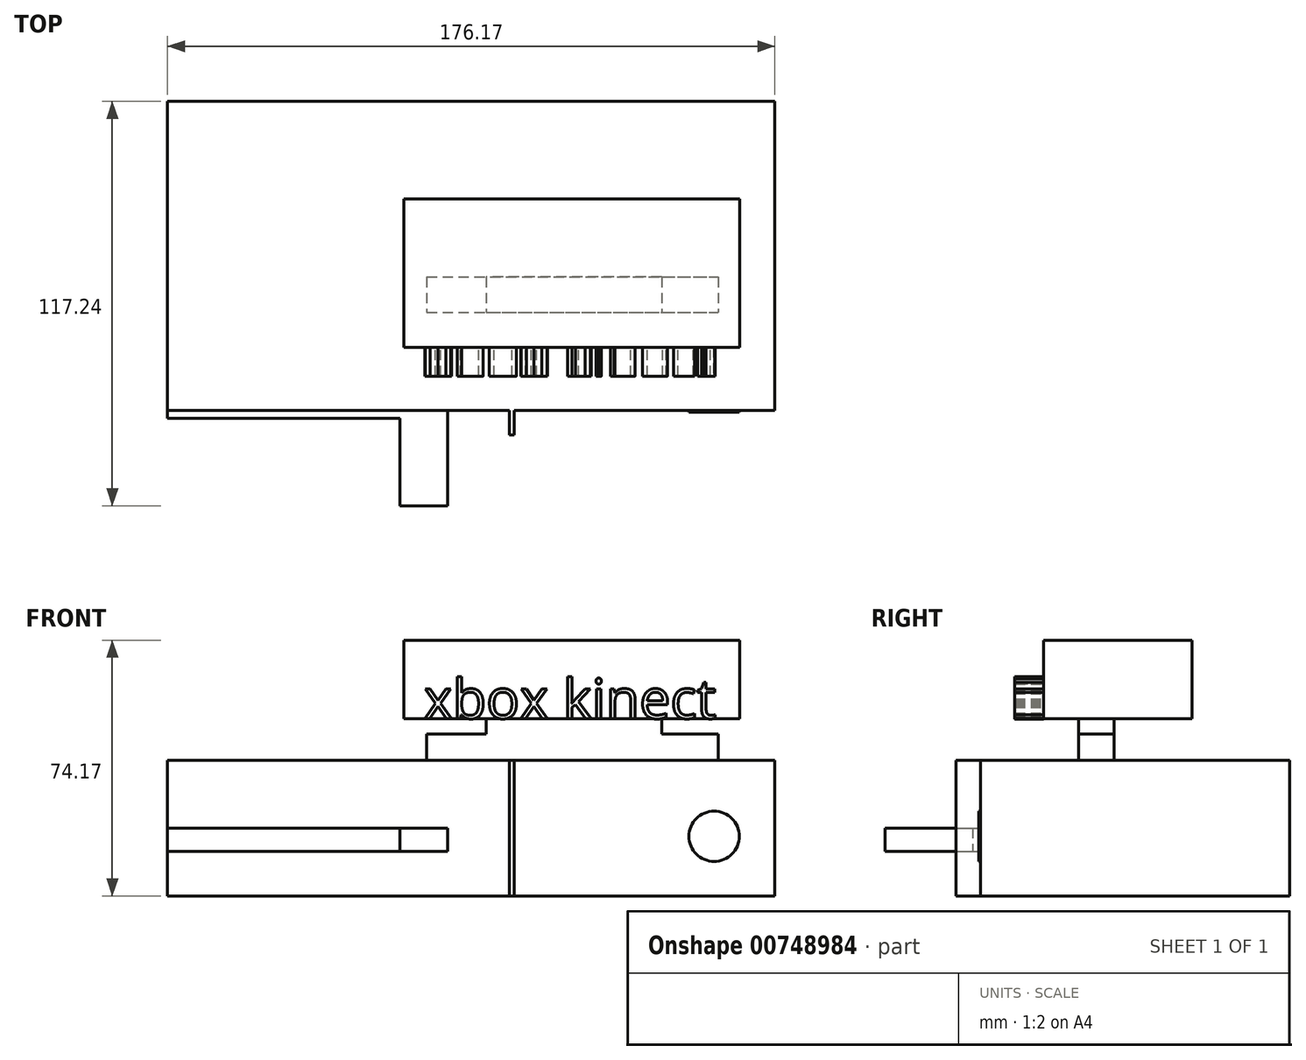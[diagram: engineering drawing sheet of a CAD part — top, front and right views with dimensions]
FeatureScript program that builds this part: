
annotation { "Feature Type Name" : "Feature", "Feature Type Description" : "" }
export const myFeature = defineFeature(function(context is Context, id is Id, definition is map)
    precondition{}
    {
        {
            var Q0;
            Q0=qCreatedBy(makeId("Top.planeOp"),FACE);
            var sketch = newSketch(context, id + "F0", { "sketchPlane" : qUnion([Q0])});
            skLineSegment(sketch, "E0.bottom", {"start": v(-150.59, 27.34) * mm, "end": v(25.58, 27.34) * mm});
            skLineSegment(sketch, "E0.top", {"start": v(-150.59, -62.22) * mm, "end": v(25.58, -62.22) * mm});
            skLineSegment(sketch, "E0.left", {"start": v(-150.59, 27.34) * mm, "end": v(-150.59, -62.22) * mm});
            skLineSegment(sketch, "E0.right", {"start": v(25.58, 27.34) * mm, "end": v(25.58, -62.22) * mm});
            skSolve(sketch);
        }
        {
            var Q0;
            Q0 = qSketchRegion(id + "F0", true);
            extrude(context, id + "F1", {"entities" : qUnion([Q0]), "depth" : 39.37 * mm, "offsetDistance" : 25.4 * mm});
        }
        {
            var Q0;
            Q0=makeQuery(id+"F1.opExtrude","SWEPT_FACE",FACE,{"disambiguationData":[OSD([sQuery(id+"F0.wireOp",EDGE,"E0.top")])]});
            var sketch = newSketch(context, id + "F2", { "sketchPlane" : qUnion([Q0])});
            skLineSegment(sketch, "E1.bottom", {"start": v(-150.59, 19.69) * mm, "end": v(-69.38, 19.69) * mm});
            skLineSegment(sketch, "E1.top", {"start": v(-150.59, 12.94) * mm, "end": v(-69.38, 12.94) * mm});
            skLineSegment(sketch, "E1.left", {"start": v(-150.59, 19.69) * mm, "end": v(-150.59, 12.94) * mm});
            skLineSegment(sketch, "E1.right", {"start": v(-69.38, 19.69) * mm, "end": v(-69.38, 12.94) * mm});
            skSolve(sketch);
        }
        {
            var Q0;
            Q0 = qSketchRegion(id + "F2", true);
            extrude(context, id + "F3", {"entities" : qUnion([Q0]), "operationType" : NewBodyOperationType.ADD, "depth" : 2.3 * mm, "offsetDistance" : 25.4 * mm});
        }
        {
            var Q0;
            Q0=makeQuery(id+"F1.opExtrude","SWEPT_FACE",FACE,{"disambiguationData":[OSD([sQuery(id+"F0.wireOp",EDGE,"E0.top")])]});
            var sketch = newSketch(context, id + "F4", { "sketchPlane" : qUnion([Q0])});
            skCircle(sketch, "E2", {"center": v(7.94, 17.3) * mm, "radius": 7.3 * mm});
            skSolve(sketch);
        }
        {
            var Q0;
            Q0 = qSketchRegion(id + "F4", true);
            extrude(context, id + "F5", {"entities" : qUnion([Q0]), "operationType" : NewBodyOperationType.ADD, "depth" : 0.5 * mm, "offsetDistance" : 25.4 * mm});
        }
        {
            var Q0;
            Q0=makeQuery(id+"F1.opExtrude","CAP_FACE",FACE,{"disambiguationData":[OSD([sQuery(id+"F0.wireOp",EDGE,"E0.bottom"),sQuery(id+"F0.wireOp",EDGE,"E0.top"),sQuery(id+"F0.wireOp",EDGE,"E0.left"),sQuery(id+"F0.wireOp",EDGE,"E0.right")])],"isStart":false});
            var sketch = newSketch(context, id + "F6", { "sketchPlane" : qUnion([Q0])});
            skText(sketch, "E3", { "text": "xbox one", "fontName": "OpenSans-Regular.ttf"});
            const initialGuessF6  = {"E3": [-0.14363, -0.05804, 1, 0, 0.0093]};
            skSetInitialGuess(sketch, initialGuessF6);
            skSolve(sketch);
        }
        {
            var Q0;
            Q0=makeQuery(id+"F6.imprint","IMPRINT",FACE,{"disambiguationData":[TD([[makeQuery(id+"F6.imprint","IMPRINT",EDGE,{"derivedFrom":sQuery(id+"F6.wireOp",EDGE,"E3.sketch_text.stroke-0")}),1.0]])]});
            var sketch = newSketch(context, id + "F7", { "sketchPlane" : qUnion([Q0])});
            skLineSegment(sketch, "E4.bottom", {"start": v(-75.4, -23.59) * mm, "end": v(9.16, -23.59) * mm});
            skLineSegment(sketch, "E4.top", {"start": v(-75.4, -33.78) * mm, "end": v(9.16, -33.78) * mm});
            skLineSegment(sketch, "E4.left", {"start": v(-75.4, -23.59) * mm, "end": v(-75.4, -33.78) * mm});
            skLineSegment(sketch, "E4.right", {"start": v(9.16, -23.59) * mm, "end": v(9.16, -33.78) * mm});
            skSolve(sketch);
        }
        {
            var Q0;
            Q0 = qSketchRegion(id + "F7", true);
            extrude(context, id + "F8", {"entities" : qUnion([Q0]), "operationType" : NewBodyOperationType.ADD, "depth" : 7.62 * mm, "offsetDistance" : 25.4 * mm});
        }
        {
            var Q0;
            Q0=makeQuery(id+"F8.opExtrude","CAP_FACE",FACE,{"disambiguationData":[OSD([sQuery(id+"F7.wireOp",EDGE,"E4.bottom"),sQuery(id+"F7.wireOp",EDGE,"E4.top"),sQuery(id+"F7.wireOp",EDGE,"E4.left"),sQuery(id+"F7.wireOp",EDGE,"E4.right")])],"isStart":false});
            var sketch = newSketch(context, id + "F9", { "sketchPlane" : qUnion([Q0])});
            skLineSegment(sketch, "E5.bottom", {"start": v(-58.14, -23.59) * mm, "end": v(-7.28, -23.59) * mm});
            skLineSegment(sketch, "E5.top", {"start": v(-58.14, -33.78) * mm, "end": v(-7.28, -33.78) * mm});
            skLineSegment(sketch, "E5.left", {"start": v(-58.14, -23.59) * mm, "end": v(-58.14, -33.78) * mm});
            skLineSegment(sketch, "E5.right", {"start": v(-7.28, -23.59) * mm, "end": v(-7.28, -33.78) * mm});
            skSolve(sketch);
        }
        {
            var Q0;
            Q0 = qSketchRegion(id + "F9", true);
            extrude(context, id + "F10", {"entities" : qUnion([Q0]), "operationType" : NewBodyOperationType.ADD, "depth" : 8.9 * mm, "offsetDistance" : 25.4 * mm});
        }
        {
            var Q0;
            Q0=makeQuery(id+"F10.boolean.opBoolean","MERGE",FACE,{"derivedFrom":[makeQuery(id+"F8.opExtrude","SWEPT_FACE",FACE,{"disambiguationData":[OSD([sQuery(id+"F7.wireOp",EDGE,"E4.top")])]}),makeQuery(id+"F10.opExtrude","SWEPT_FACE",FACE,{"disambiguationData":[OSD([sQuery(id+"F9.wireOp",EDGE,"E5.top")])]})]});
            var sketch = newSketch(context, id + "F11", { "sketchPlane" : qUnion([Q0])});
            skLineSegment(sketch, "E6.bottom", {"start": v(-58.14, 51.44) * mm, "end": v(-7.28, 51.44) * mm});
            skLineSegment(sketch, "E6.top", {"start": v(-58.14, 55.88) * mm, "end": v(-7.28, 55.88) * mm});
            skLineSegment(sketch, "E6.left", {"start": v(-58.14, 51.44) * mm, "end": v(-58.14, 55.88) * mm});
            skLineSegment(sketch, "E6.right", {"start": v(-7.28, 51.44) * mm, "end": v(-7.28, 55.88) * mm});
            skSolve(sketch);
        }
        {
            var Q0;
            Q0 = qSketchRegion(id + "F11", true);
            extrude(context, id + "F12", {"entities" : qUnion([Q0]), "operationType" : NewBodyOperationType.ADD, "depth" : 10.16 * mm, "offsetDistance" : 25.4 * mm});
        }
        {
            var Q0;
            Q0=makeQuery(id+"F10.boolean.opBoolean","MERGE",FACE,{"derivedFrom":[makeQuery(id+"F8.opExtrude","SWEPT_FACE",FACE,{"disambiguationData":[OSD([sQuery(id+"F7.wireOp",EDGE,"E4.bottom")])]}),makeQuery(id+"F10.opExtrude","SWEPT_FACE",FACE,{"disambiguationData":[OSD([sQuery(id+"F9.wireOp",EDGE,"E5.bottom")])]})]});
            var sketch = newSketch(context, id + "F13", { "sketchPlane" : qUnion([Q0])});
            skLineSegment(sketch, "E7.bottom", {"start": v(7.28, 51.44) * mm, "end": v(58.14, 51.44) * mm});
            skLineSegment(sketch, "E7.top", {"start": v(7.28, 55.88) * mm, "end": v(58.14, 55.88) * mm});
            skLineSegment(sketch, "E7.left", {"start": v(7.28, 51.44) * mm, "end": v(7.28, 55.88) * mm});
            skLineSegment(sketch, "E7.right", {"start": v(58.14, 51.44) * mm, "end": v(58.14, 55.88) * mm});
            skSolve(sketch);
        }
        {
            var Q0;
            Q0 = qSketchRegion(id + "F13", true);
            extrude(context, id + "F14", {"entities" : qUnion([Q0]), "operationType" : NewBodyOperationType.ADD, "depth" : 22.6 * mm, "offsetDistance" : 25.4 * mm});
        }
        {
            var Q0;
            Q0=makeQuery(id+"F14.boolean.opBoolean","MERGE",FACE,{"derivedFrom":[makeQuery(id+"F12.boolean.opBoolean","MERGE",FACE,{"derivedFrom":[makeQuery(id+"F10.opExtrude","CAP_FACE",FACE,{"disambiguationData":[OSD([sQuery(id+"F9.wireOp",EDGE,"E5.bottom"),sQuery(id+"F9.wireOp",EDGE,"E5.top"),sQuery(id+"F9.wireOp",EDGE,"E5.left"),sQuery(id+"F9.wireOp",EDGE,"E5.right")])],"isStart":false}),makeQuery(id+"F12.opExtrude","SWEPT_FACE",FACE,{"disambiguationData":[OSD([sQuery(id+"F11.wireOp",EDGE,"E6.top")])]})]}),makeQuery(id+"F14.opExtrude","SWEPT_FACE",FACE,{"disambiguationData":[OSD([sQuery(id+"F13.wireOp",EDGE,"E7.top")])]})]});
            extrude(context, id + "F15", {"entities" : qUnion([Q0]), "operationType" : NewBodyOperationType.ADD, "depth" : 18.29 * mm, "offsetDistance" : 25.4 * mm});
        }
        {
            var Q0;
            {var subQ0=sQuery(id+"F13.wireOp",EDGE,"E7.left");var subQ1=sQuery(id+"F11.wireOp",EDGE,"E6.right");var subQ2=sQuery(id+"F9.wireOp",EDGE,"E5.right");Q0=makeQuery(id+"F15.boolean.opBoolean","MERGE",FACE,{"derivedFrom":[makeQuery(id+"F14.boolean.opBoolean","MERGE",FACE,{"derivedFrom":[makeQuery(id+"F12.boolean.opBoolean","MERGE",FACE,{"derivedFrom":[makeQuery(id+"F10.opExtrude","SWEPT_FACE",FACE,{"disambiguationData":[OSD([subQ2])]}),makeQuery(id+"F12.opExtrude","SWEPT_FACE",FACE,{"disambiguationData":[OSD([subQ1])]})]}),makeQuery(id+"F14.opExtrude","SWEPT_FACE",FACE,{"disambiguationData":[OSD([subQ0])]})]}),makeQuery(id+"F15.opExtrude","SWEPT_FACE",FACE,{"disambiguationData":[OSD([subQ2,sQuery(id+"F11.wireOp",EDGE,"E6.top"),subQ1,sQuery(id+"F13.wireOp",EDGE,"E7.top"),subQ0])]})]});}
            var sketch = newSketch(context, id + "F16", { "sketchPlane" : qUnion([Q0])});
            skLineSegment(sketch, "E8.bottom", {"start": v(-43.94, 74.17) * mm, "end": v(-0.98, 74.17) * mm});
            skLineSegment(sketch, "E8.top", {"start": v(-43.94, 51.44) * mm, "end": v(-0.98, 51.44) * mm});
            skLineSegment(sketch, "E8.left", {"start": v(-43.94, 74.17) * mm, "end": v(-43.94, 51.44) * mm});
            skLineSegment(sketch, "E8.right", {"start": v(-0.98, 74.17) * mm, "end": v(-0.98, 51.44) * mm});
            skSolve(sketch);
        }
        {
            var Q0;
            Q0 = qSketchRegion(id + "F16", true);
            extrude(context, id + "F17", {"entities" : qUnion([Q0]), "operationType" : NewBodyOperationType.ADD, "depth" : 22.6 * mm, "offsetDistance" : 25.4 * mm});
        }
        {
            var Q0;
            {var subQ0=sQuery(id+"F13.wireOp",EDGE,"E7.right");var subQ1=sQuery(id+"F11.wireOp",EDGE,"E6.left");var subQ2=sQuery(id+"F9.wireOp",EDGE,"E5.left");Q0=makeQuery(id+"F15.boolean.opBoolean","MERGE",FACE,{"derivedFrom":[makeQuery(id+"F14.boolean.opBoolean","MERGE",FACE,{"derivedFrom":[makeQuery(id+"F12.boolean.opBoolean","MERGE",FACE,{"derivedFrom":[makeQuery(id+"F10.opExtrude","SWEPT_FACE",FACE,{"disambiguationData":[OSD([subQ2])]}),makeQuery(id+"F12.opExtrude","SWEPT_FACE",FACE,{"disambiguationData":[OSD([subQ1])]})]}),makeQuery(id+"F14.opExtrude","SWEPT_FACE",FACE,{"disambiguationData":[OSD([subQ0])]})]}),makeQuery(id+"F15.opExtrude","SWEPT_FACE",FACE,{"disambiguationData":[OSD([subQ2,sQuery(id+"F11.wireOp",EDGE,"E6.top"),subQ1,sQuery(id+"F13.wireOp",EDGE,"E7.top"),subQ0])]})]});}
            var sketch = newSketch(context, id + "F18", { "sketchPlane" : qUnion([Q0])});
            skLineSegment(sketch, "E9.bottom", {"start": v(0.98, 74.17) * mm, "end": v(43.94, 74.17) * mm});
            skLineSegment(sketch, "E9.top", {"start": v(0.98, 51.44) * mm, "end": v(43.94, 51.44) * mm});
            skLineSegment(sketch, "E9.left", {"start": v(0.98, 74.17) * mm, "end": v(0.98, 51.44) * mm});
            skLineSegment(sketch, "E9.right", {"start": v(43.94, 74.17) * mm, "end": v(43.94, 51.44) * mm});
            skSolve(sketch);
        }
        {
            var Q0;
            Q0 = qSketchRegion(id + "F18", true);
            extrude(context, id + "F19", {"entities" : qUnion([Q0]), "operationType" : NewBodyOperationType.ADD, "depth" : 23.88 * mm, "offsetDistance" : 25.4 * mm});
        }
        {
            var Q0;
            {var subQ0=sQuery(id+"F11.wireOp",EDGE,"E6.top");Q0=makeQuery(id+"F19.boolean.opBoolean","MERGE",FACE,{"derivedFrom":[makeQuery(id+"F17.boolean.opBoolean","MERGE",FACE,{"derivedFrom":[makeQuery(id+"F15.boolean.opBoolean","MERGE",FACE,{"derivedFrom":[makeQuery(id+"F12.opExtrude","CAP_FACE",FACE,{"disambiguationData":[OSD([sQuery(id+"F11.wireOp",EDGE,"E6.bottom"),subQ0,sQuery(id+"F11.wireOp",EDGE,"E6.left"),sQuery(id+"F11.wireOp",EDGE,"E6.right")])],"isStart":false}),makeQuery(id+"F15.opExtrude","SWEPT_FACE",FACE,{"disambiguationData":[OSD([subQ0])]})]}),makeQuery(id+"F17.opExtrude","SWEPT_FACE",FACE,{"disambiguationData":[OSD([sQuery(id+"F16.wireOp",EDGE,"E8.left")])]})]}),makeQuery(id+"F19.opExtrude","SWEPT_FACE",FACE,{"disambiguationData":[OSD([sQuery(id+"F18.wireOp",EDGE,"E9.right")])]})]});}
            var sketch = newSketch(context, id + "F20", { "sketchPlane" : qUnion([Q0])});
            skText(sketch, "E10", { "text": "xbox kinect", "fontName": "OpenSans-Regular.ttf"});
            const initialGuessF20  = {"E10": [-0.07631, 0.05144, 1, 0, 0.01151]};
            skSetInitialGuess(sketch, initialGuessF20);
            skSolve(sketch);
        }
        {
            var Q0;
            Q0 = qSketchRegion(id + "F20", true);
            extrude(context, id + "F21", {"entities" : qUnion([Q0]), "operationType" : NewBodyOperationType.ADD, "depth" : 8.38 * mm, "offsetDistance" : 25.4 * mm});
        }
        {
            var Q0;
            Q0=makeQuery(id+"F1.opExtrude","SWEPT_FACE",FACE,{"disambiguationData":[OSD([sQuery(id+"F0.wireOp",EDGE,"E0.top")])]});
            var sketch = newSketch(context, id + "F22", { "sketchPlane" : qUnion([Q0])});
            skText(sketch, "E11", { "text": "xbox one", "fontName": "OpenSans-Regular.ttf"});
            const initialGuessF22  = {"E11": [-0.1451, 0.02439, 1, 0, 0.00878]};
            skSetInitialGuess(sketch, initialGuessF22);
            skSolve(sketch);
        }
        {
            var Q0;
            {var subQ0=sQuery(id+"F0.wireOp",EDGE,"E0.left");var subQ2=sQuery(id+"F0.wireOp",EDGE,"E0.top");Q0=makeQuery(id+"FrHqVm97nXn3FNT_1.boolean.opBoolean","SPLIT",FACE,{"disambiguationData":[TD([makeQuery(id+"F1.opExtrude","SWEPT_FACE",FACE,{"disambiguationData":[OSD([subQ0])]})])],"derivedFrom":makeQuery(id+"F1.opExtrude","SWEPT_FACE",FACE,{"disambiguationData":[OSD([subQ2])]})});}
            var sketch = newSketch(context, id + "F23", { "sketchPlane" : qUnion([Q0])});
            skLineSegment(sketch, "E12.bottom", {"start": v(-50.11, 39.37) * mm, "end": v(-51.4, 39.37) * mm});
            skLineSegment(sketch, "E12.top", {"start": v(-50.11, 0) * mm, "end": v(-51.4, 0) * mm});
            skLineSegment(sketch, "E12.left", {"start": v(-50.11, 39.37) * mm, "end": v(-50.11, 0) * mm});
            skLineSegment(sketch, "E12.right", {"start": v(-51.4, 39.37) * mm, "end": v(-51.4, 0) * mm});
            skSolve(sketch);
        }
        {
            var Q0;
            Q0 = qSketchRegion(id + "F23", true);
            extrude(context, id + "F24", {"entities" : qUnion([Q0]), "operationType" : NewBodyOperationType.ADD, "depth" : 7.11 * mm, "offsetDistance" : 25.4 * mm});
        }
        {
            var Q0;
            Q0 = qSketchRegion(id + "F22", true);
            extrude(context, id + "F25", {"entities" : qUnion([Q0]), "operationType" : NewBodyOperationType.ADD, "oppositeDirection" : true, "depth" : 2.3 * mm, "offsetDistance" : 25.4 * mm});
        }
        {
            var Q0;
            {var subQ1=sQuery(id+"F0.wireOp",EDGE,"E0.left");var subQ2=sQuery(id+"F0.wireOp",EDGE,"E0.top");Q0=makeQuery(id+"F24.boolean.opBoolean","SPLIT",FACE,{"disambiguationData":[TD([makeQuery(id+"F1.opExtrude","SWEPT_FACE",FACE,{"disambiguationData":[OSD([subQ1])]})])],"derivedFrom":makeQuery(id+"F1.opExtrude","SWEPT_FACE",FACE,{"disambiguationData":[OSD([subQ2])]})});}
            var sketch = newSketch(context, id + "F26", { "sketchPlane" : qUnion([Q0])});
            skText(sketch, "E13", { "text": "xbox one\n", "fontName": "OpenSans-Regular.ttf"});
            const initialGuessF26  = {"E13": [-0.14469, 0.02415, 1, 0, 0.00927]};
            skSetInitialGuess(sketch, initialGuessF26);
            skSolve(sketch);
        }
        {
            var Q0;
            Q0 = qSketchRegion(id + "F26", true);
            extrude(context, id + "F27", {"entities" : qUnion([Q0]), "operationType" : NewBodyOperationType.ADD, "flatOperationType" : FlatOperationType.REMOVE, "oppositeDirection" : true, "depth" : 2.3 * mm, "offsetDistance" : 25.4 * mm, "domain" : OperationDomain.MODEL});
        }
        {
            var Q0;
            Q0=makeQuery(id+"F3.opExtrude","CAP_FACE",FACE,{"disambiguationData":[OSD([sQuery(id+"F2.wireOp",EDGE,"E1.bottom"),sQuery(id+"F2.wireOp",EDGE,"E1.top"),sQuery(id+"F2.wireOp",EDGE,"E1.left"),sQuery(id+"F2.wireOp",EDGE,"E1.right")])],"isStart":false});
            var sketch = newSketch(context, id + "F28", { "sketchPlane" : qUnion([Q0])});
            skLineSegment(sketch, "E14.bottom", {"start": v(-83.18, 19.69) * mm, "end": v(-69.38, 19.69) * mm});
            skLineSegment(sketch, "E14.top", {"start": v(-83.18, 12.94) * mm, "end": v(-69.38, 12.94) * mm});
            skLineSegment(sketch, "E14.left", {"start": v(-83.18, 19.69) * mm, "end": v(-83.18, 12.94) * mm});
            skLineSegment(sketch, "E14.right", {"start": v(-69.38, 19.69) * mm, "end": v(-69.38, 12.94) * mm});
            skSolve(sketch);
        }
        {
            var Q0;
            Q0 = qSketchRegion(id + "F28", true);
            extrude(context, id + "F29", {"entities" : qUnion([Q0]), "operationType" : NewBodyOperationType.ADD, "depth" : 25.4 * mm, "offsetDistance" : 25.4 * mm});
        }
    });
